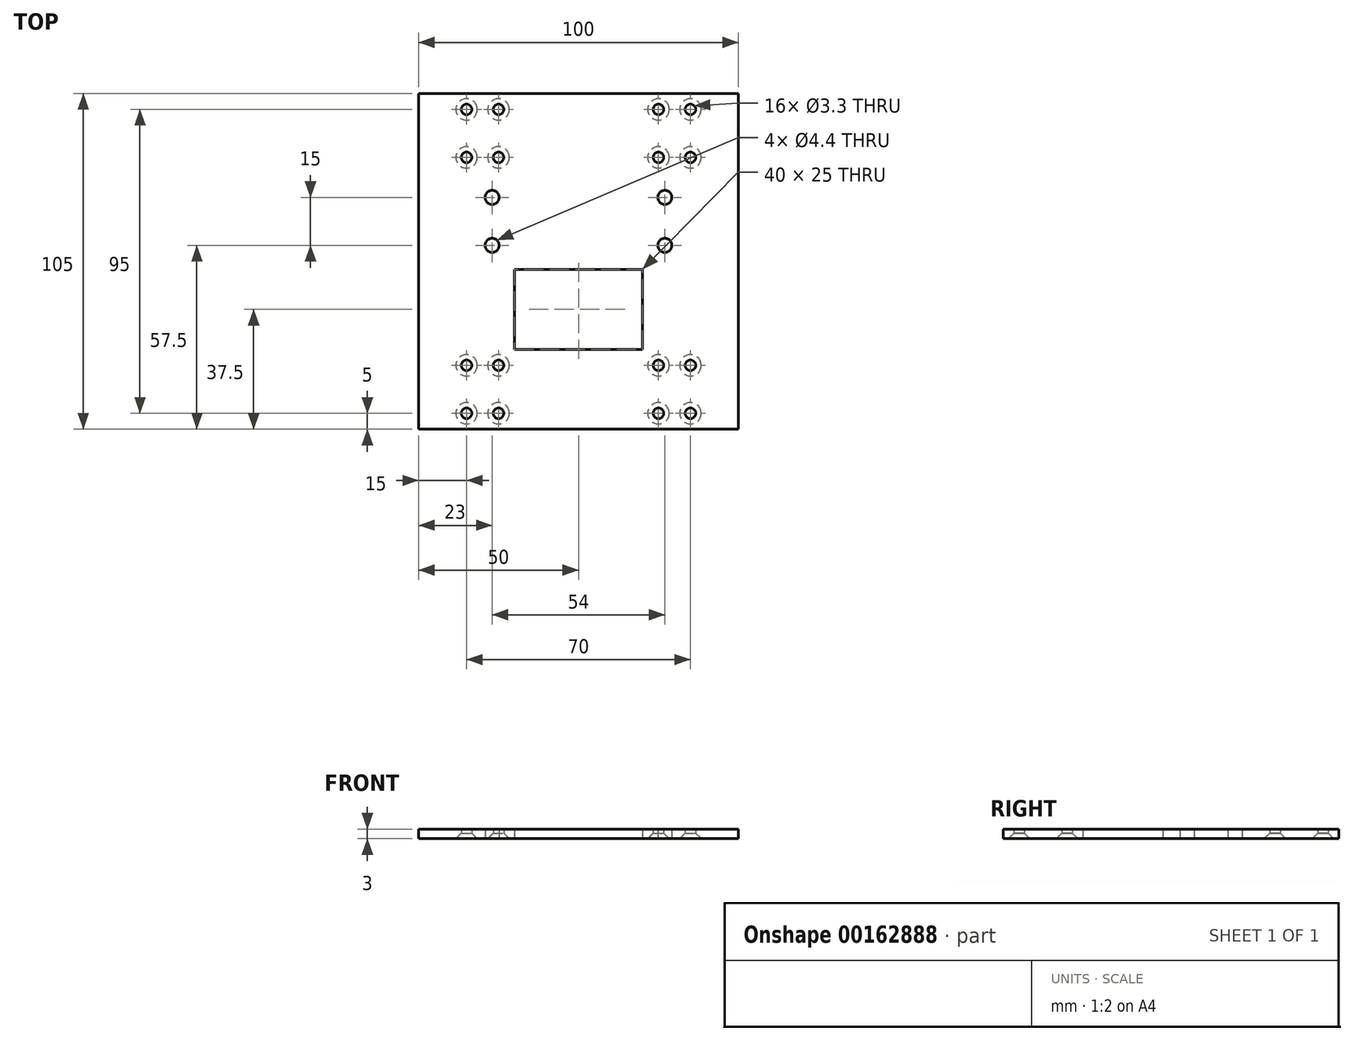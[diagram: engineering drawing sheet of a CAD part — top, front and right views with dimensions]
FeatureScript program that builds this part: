
annotation { "Feature Type Name" : "Feature", "Feature Type Description" : "" }
export const myFeature = defineFeature(function(context is Context, id is Id, definition is map)
    precondition{}
    {
        {
            var Q0;
            Q0=qCreatedBy(makeId("Top.planeOp"),FACE);
            var sketch = newSketch(context, id + "F0", { "sketchPlane" : qUnion([Q0])});
            skLineSegment(sketch, "E0.bottom", {"start": v(50, -52.5) * mm, "end": v(-50, -52.5) * mm});
            skLineSegment(sketch, "E0.top", {"start": v(50, 52.5) * mm, "end": v(-50, 52.5) * mm});
            skLineSegment(sketch, "E0.left", {"start": v(50, -52.5) * mm, "end": v(50, 52.5) * mm});
            skLineSegment(sketch, "E0.right", {"start": v(-50, -52.5) * mm, "end": v(-50, 52.5) * mm});
            skPoint(sketch, "E0.middle", {"position": v(0, 0) * mm});
            skLineSegment(sketch, "E1.bottom", {"start": v(-25, 32.5) * mm, "end": v(-35, 32.5) * mm, "construction": true});
            skLineSegment(sketch, "E1.top", {"start": v(-25, 47.5) * mm, "end": v(-35, 47.5) * mm, "construction": true});
            skLineSegment(sketch, "E1.left", {"start": v(-25, 32.5) * mm, "end": v(-25, 47.5) * mm, "construction": true});
            skLineSegment(sketch, "E1.right", {"start": v(-35, 32.5) * mm, "end": v(-35, 47.5) * mm, "construction": true});
            skPoint(sketch, "E1.middle", {"position": v(-30, 40) * mm});
            skLineSegment(sketch, "E2.MirrorCS", {"start": v(25, 32.5) * mm, "end": v(25, 47.5) * mm, "construction": true});
            skLineSegment(sketch, "E3.MirrorCS", {"start": v(25, 47.5) * mm, "end": v(35, 47.5) * mm, "construction": true});
            skLineSegment(sketch, "E4.MirrorCS", {"start": v(35, 32.5) * mm, "end": v(35, 47.5) * mm, "construction": true});
            skLineSegment(sketch, "E5.MirrorCS", {"start": v(25, 32.5) * mm, "end": v(35, 32.5) * mm, "construction": true});
            skLineSegment(sketch, "E6.MirrorCS", {"start": v(-25, -32.5) * mm, "end": v(-35, -32.5) * mm, "construction": true});
            skLineSegment(sketch, "E7.MirrorCS", {"start": v(-35, -32.5) * mm, "end": v(-35, -47.5) * mm, "construction": true});
            skLineSegment(sketch, "E8.MirrorCS", {"start": v(-25, -47.5) * mm, "end": v(-35, -47.5) * mm, "construction": true});
            skLineSegment(sketch, "E9.MirrorCS", {"start": v(-25, -32.5) * mm, "end": v(-25, -47.5) * mm, "construction": true});
            skLineSegment(sketch, "E10.MirrorCS", {"start": v(25, -32.5) * mm, "end": v(25, -47.5) * mm, "construction": true});
            skLineSegment(sketch, "E11.MirrorCS", {"start": v(25, -47.5) * mm, "end": v(35, -47.5) * mm, "construction": true});
            skLineSegment(sketch, "E12.MirrorCS", {"start": v(35, -32.5) * mm, "end": v(35, -47.5) * mm, "construction": true});
            skLineSegment(sketch, "E13.MirrorCS", {"start": v(25, -32.5) * mm, "end": v(35, -32.5) * mm, "construction": true});
            skPoint(sketch, "E14", {"position": v(-27, 20) * mm});
            skPoint(sketch, "E15", {"position": v(-27, 5) * mm});
            skPoint(sketch, "E16.MirrorP", {"position": v(27, 5) * mm});
            skPoint(sketch, "E17.MirrorP", {"position": v(27, 20) * mm});
            skLineSegment(sketch, "E18.bottom", {"start": v(20, -2.5) * mm, "end": v(-20, -2.5) * mm});
            skLineSegment(sketch, "E18.top", {"start": v(20, -27.5) * mm, "end": v(-20, -27.5) * mm});
            skLineSegment(sketch, "E18.left", {"start": v(20, -2.5) * mm, "end": v(20, -27.5) * mm});
            skLineSegment(sketch, "E18.right", {"start": v(-20, -2.5) * mm, "end": v(-20, -27.5) * mm});
            skPoint(sketch, "E18.middle", {"position": v(0, -15) * mm});
            skSolve(sketch);
        }
        {
            var Q0;
            Q0=makeQuery(id+"F0.imprint","IMPRINT",FACE,{"disambiguationData":[TD([[makeQuery(id+"F0.imprint","IMPRINT",EDGE,{"derivedFrom":sQuery(id+"F0.wireOp",EDGE,"E0.bottom")}),-1.0]])]});
            extrude(context, id + "F1", {"entities" : qUnion([Q0]), "depth" : 3 * mm, "offsetDistance" : 25 * mm});
        }
        {
            var Q0;
            Q0=sQuery(id+"F0.wireOp",VERTEX,"E1.bottom.end");
            var Q1;
            Q1=sQuery(id+"F0.wireOp",VERTEX,"E1.bottom.start");
            var Q2;
            Q2=sQuery(id+"F0.wireOp",VERTEX,"E1.top.start");
            var Q3;
            Q3=sQuery(id+"F0.wireOp",VERTEX,"E1.top.end");
            var Q4;
            Q4=sQuery(id+"F0.wireOp",VERTEX,"E2.MirrorCS.end");
            var Q5;
            Q5=sQuery(id+"F0.wireOp",VERTEX,"E2.MirrorCS.start");
            var Q6;
            Q6=sQuery(id+"F0.wireOp",VERTEX,"E4.MirrorCS.start");
            var Q7;
            Q7=sQuery(id+"F0.wireOp",VERTEX,"E3.MirrorCS.end");
            var Q8;
            Q8=sQuery(id+"F0.wireOp",VERTEX,"E10.MirrorCS.start");
            var Q9;
            Q9=sQuery(id+"F0.wireOp",VERTEX,"E12.MirrorCS.start");
            var Q10;
            Q10=sQuery(id+"F0.wireOp",VERTEX,"E11.MirrorCS.end");
            var Q11;
            Q11=sQuery(id+"F0.wireOp",VERTEX,"E10.MirrorCS.end");
            var Q12;
            Q12=sQuery(id+"F0.wireOp",VERTEX,"E8.MirrorCS.start");
            var Q13;
            Q13=sQuery(id+"F0.wireOp",VERTEX,"E7.MirrorCS.end");
            var Q14;
            Q14=sQuery(id+"F0.wireOp",VERTEX,"E6.MirrorCS.end");
            var Q15;
            Q15=sQuery(id+"F0.wireOp",VERTEX,"E6.MirrorCS.start");
            var Q16;
            Q16=makeQuery(id+"F1.opExtrude","SWEPT_BODY",BODY,{"disambiguationData":[OSD([sQuery(id+"F0.wireOp",EDGE,"E0.bottom"),sQuery(id+"F0.wireOp",EDGE,"E0.top"),sQuery(id+"F0.wireOp",EDGE,"E0.left"),sQuery(id+"F0.wireOp",EDGE,"E0.right")])]});
            hole(context, id + "F2", {"style" : HoleStyle.C_SINK, "endStyle" : HoleEndStyle.THROUGH, "oppositeDirection" : true, "standardTappedOrClearance" : lookupTablePath({ "standard" : "ISO", "fit" : "Normal", "size" : "M3", "type" : "Clearance" }), "standardBlindInLast" : lookupTablePath({ "fit" : "Standard", "standard" : "ISO", "size" : "M3", "type" : "Clearance" }), "holeDiameter" : 3.3 * mm, "cSinkDiameter" : 6.72 * mm, "cSinkAngle" : 90 * degree, "majorDiameter" : 3 * mm, "isTappedThrough" : true, "tappedDepth" : 4 * mm, "tapClearance" : 3, "startFromSketch" : true, "locations" : qUnion([Q0, Q1, Q2, Q3, Q4, Q5, Q6, Q7, Q8, Q9, Q10, Q11, Q12, Q13, Q14, Q15]), "scope" : qUnion([Q16])});
        }
        {
            var Q0;
            Q0=sQuery(id+"F0.wireOp",VERTEX,"E16.MirrorP");
            var Q1;
            Q1=sQuery(id+"F0.wireOp",VERTEX,"E17.MirrorP");
            var Q2;
            Q2=sQuery(id+"F0.wireOp",VERTEX,"E15");
            var Q3;
            Q3=sQuery(id+"F0.wireOp",VERTEX,"E14");
            var Q4;
            Q4=makeQuery(id+"F1.opExtrude","SWEPT_BODY",BODY,{"disambiguationData":[OSD([sQuery(id+"F0.wireOp",EDGE,"E0.bottom"),sQuery(id+"F0.wireOp",EDGE,"E0.top"),sQuery(id+"F0.wireOp",EDGE,"E0.left"),sQuery(id+"F0.wireOp",EDGE,"E0.right")])]});
            hole(context, id + "F3", {"style" : HoleStyle.SIMPLE, "endStyle" : HoleEndStyle.THROUGH, "oppositeDirection" : true, "standardTappedOrClearance" : lookupTablePath({ "standard" : "ISO", "fit" : "Normal", "size" : "M4", "type" : "Clearance" }), "standardBlindInLast" : lookupTablePath({ "fit" : "Standard", "standard" : "ISO", "size" : "M4", "type" : "Clearance" }), "holeDiameter" : 4.4 * mm, "majorDiameter" : 5 * mm, "isTappedThrough" : true, "tappedDepth" : 4 * mm, "tapClearance" : 3, "startFromSketch" : true, "locations" : qUnion([Q0, Q1, Q2, Q3]), "scope" : qUnion([Q4])});
        }
    });
